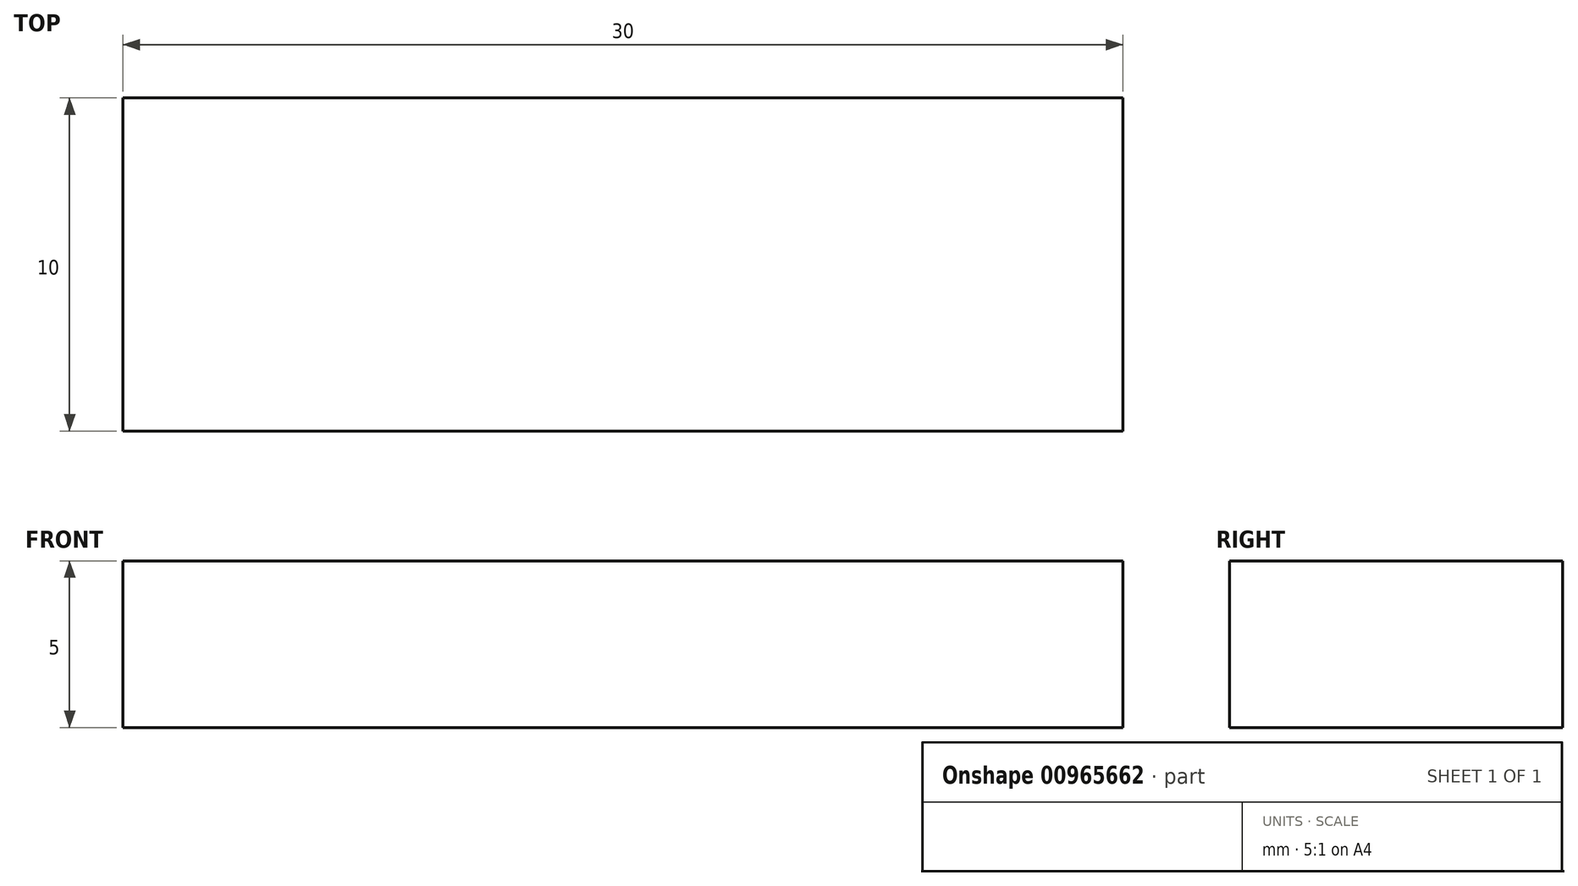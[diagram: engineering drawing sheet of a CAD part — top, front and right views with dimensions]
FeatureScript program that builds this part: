
annotation { "Feature Type Name" : "Feature", "Feature Type Description" : "" }
export const myFeature = defineFeature(function(context is Context, id is Id, definition is map)
    precondition{}
    {
        {
            var Q0;
            Q0=qCreatedBy(makeId("Top.planeOp"),FACE);
            var sketch = newSketch(context, id + "F0", { "sketchPlane" : qUnion([Q0])});
            skLineSegment(sketch, "E0.bottom", {"start": v(15, -5) * mm, "end": v(-15, -5) * mm});
            skLineSegment(sketch, "E0.top", {"start": v(15, 5) * mm, "end": v(-15, 5) * mm});
            skLineSegment(sketch, "E0.left", {"start": v(15, -5) * mm, "end": v(15, 5) * mm});
            skLineSegment(sketch, "E0.right", {"start": v(-15, -5) * mm, "end": v(-15, 5) * mm});
            skPoint(sketch, "E0.middle", {"position": v(0, 0) * mm});
            skSolve(sketch);
        }
        {
            var Q0;
            Q0=makeQuery(id+"F0.imprint","IMPRINT",FACE,{"disambiguationData":[TD([[makeQuery(id+"F0.imprint","IMPRINT",EDGE,{"derivedFrom":sQuery(id+"F0.wireOp",EDGE,"E0.bottom")}),-1.0]])]});
            extrude(context, id + "F1", {"entities" : qUnion([Q0]), "depth" : 5 * mm, "offsetDistance" : 25 * mm});
        }
    });
